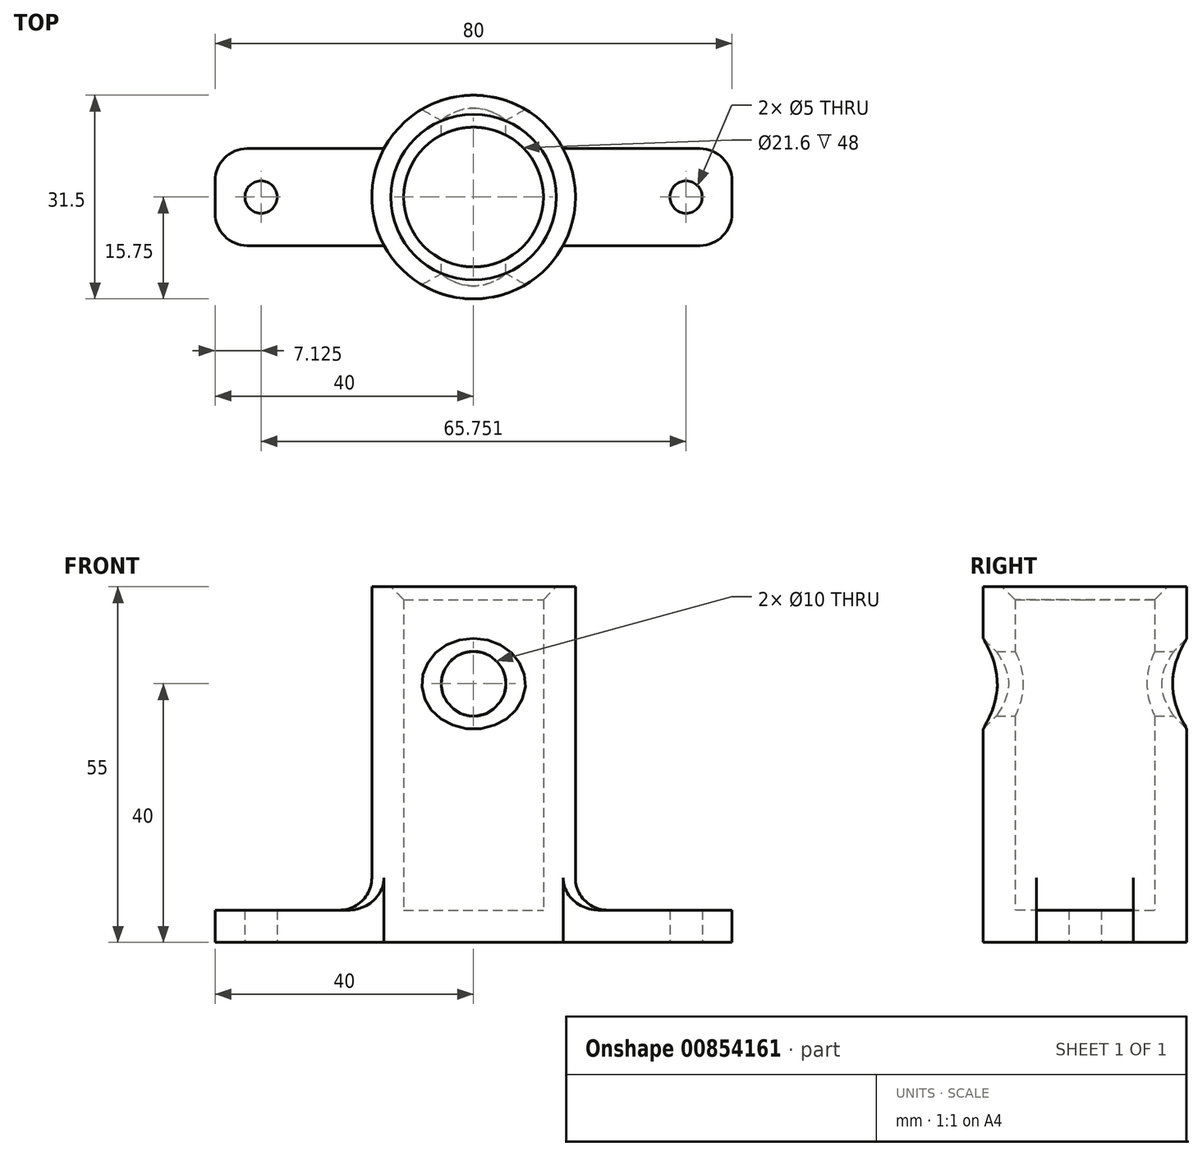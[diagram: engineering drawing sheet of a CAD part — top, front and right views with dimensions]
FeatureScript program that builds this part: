
annotation { "Feature Type Name" : "Feature", "Feature Type Description" : "" }
export const myFeature = defineFeature(function(context is Context, id is Id, definition is map)
    precondition{}
    {
        {
            var Q0;
            Q0=qCreatedBy(makeId("Top.planeOp"),FACE);
            var sketch = newSketch(context, id + "F0", { "sketchPlane" : qUnion([Q0])});
            skCircle(sketch, "E0", {"center": v(0, 0) * mm, "radius": 10.75 * mm});
            skCircle(sketch, "E1.0", {"center": v(0, 0) * mm, "radius": 15.75 * mm});
            skLineSegment(sketch, "E2.bottom", {"start": v(35, -7.5) * mm, "end": v(-35, -7.5) * mm});
            skLineSegment(sketch, "E2.top", {"start": v(35, 7.5) * mm, "end": v(-35, 7.5) * mm});
            skLineSegment(sketch, "E2.left", {"start": v(40, -2.5) * mm, "end": v(40, 2.5) * mm});
            skLineSegment(sketch, "E2.right", {"start": v(-40, -2.5) * mm, "end": v(-40, 2.5) * mm});
            skPoint(sketch, "E3.visualSharp", {"position": v(-40, 7.5) * mm});
            skArc(sketch, "E3.filletArc", {"start": v(-35, 7.5) * mm, "mid": v(-38.54, 6.04) * mm, "end": v(-40, 2.5) * mm});
            skPoint(sketch, "E4.visualSharp", {"position": v(-40, -7.5) * mm});
            skArc(sketch, "E4.filletArc", {"start": v(-40, -2.5) * mm, "mid": v(-38.54, -6.04) * mm, "end": v(-35, -7.5) * mm});
            skPoint(sketch, "E5.visualSharp", {"position": v(40, 7.5) * mm});
            skArc(sketch, "E5.filletArc", {"start": v(40, 2.5) * mm, "mid": v(38.54, 6.04) * mm, "end": v(35, 7.5) * mm});
            skPoint(sketch, "E6.visualSharp", {"position": v(40, -7.5) * mm});
            skArc(sketch, "E6.filletArc", {"start": v(35, -7.5) * mm, "mid": v(38.54, -6.04) * mm, "end": v(40, -2.5) * mm});
            skCircle(sketch, "E7", {"center": v(-32.88, 0) * mm, "radius": 2.5 * mm});
            skCircle(sketch, "E8.MirrorC", {"center": v(32.88, 0) * mm, "radius": 2.5 * mm});
            skSolve(sketch);
        }
        {
            var Q0;
            Q0 = qSketchRegion(id + "F0", true);
            var Q1;
            {var subQ0=sQuery(id+"F0.wireOp",EDGE,"E2.top");var subQ1=sQuery(id+"F0.wireOp",EDGE,"E0");var subQ2=makeQuery(id+"F0.imprint","INTERSECT",VERTEX,{"disambiguationData":[OD(0.0)],"derivedFrom":[subQ1,subQ0]});Q1=makeQuery(id+"F0.imprint","IMPRINT",FACE,{"disambiguationData":[TD([[makeQuery(id+"F0.imprint","IMPRINT",EDGE,{"disambiguationData":[TD([[subQ2,-1.0]])],"derivedFrom":subQ1}),1.0]])]});}
            var Q2;
            {var subQ0=sQuery(id+"F0.wireOp",EDGE,"E2.top");var subQ1=sQuery(id+"F0.wireOp",EDGE,"E0");var subQ2=makeQuery(id+"F0.imprint","INTERSECT",VERTEX,{"disambiguationData":[OD(0.0)],"derivedFrom":[subQ1,subQ0]});Q2=makeQuery(id+"F0.imprint","IMPRINT",FACE,{"disambiguationData":[TD([[makeQuery(id+"F0.imprint","IMPRINT",EDGE,{"disambiguationData":[TD([[subQ2,1.0]])],"derivedFrom":subQ1}),1.0]])]});}
            var Q3;
            {var subQ0=sQuery(id+"F0.wireOp",EDGE,"E2.bottom");var subQ1=sQuery(id+"F0.wireOp",EDGE,"E0");var subQ2=makeQuery(id+"F0.imprint","INTERSECT",VERTEX,{"disambiguationData":[OD(0.0)],"derivedFrom":[subQ1,subQ0]});Q3=makeQuery(id+"F0.imprint","IMPRINT",FACE,{"disambiguationData":[TD([[makeQuery(id+"F0.imprint","IMPRINT",EDGE,{"disambiguationData":[TD([[subQ2,-1.0]])],"derivedFrom":subQ1}),1.0]])]});}
            extrude(context, id + "F1", {"entities" : qUnion([Q0, Q1, Q2, Q3]), "depth" : 5 * mm, "offsetDistance" : 25 * mm});
        }
        {
            var Q0;
            Q0=makeQuery(id+"F1.opExtrude","CAP_FACE",FACE,{"disambiguationData":[OSD([sQuery(id+"F0.wireOp",EDGE,"E1.0"),sQuery(id+"F0.wireOp",EDGE,"E2.bottom"),sQuery(id+"F0.wireOp",EDGE,"E2.top"),sQuery(id+"F0.wireOp",EDGE,"E2.left"),sQuery(id+"F0.wireOp",EDGE,"E2.right"),sQuery(id+"F0.wireOp",EDGE,"E3.filletArc"),sQuery(id+"F0.wireOp",EDGE,"E4.filletArc"),sQuery(id+"F0.wireOp",EDGE,"E5.filletArc"),sQuery(id+"F0.wireOp",EDGE,"E6.filletArc"),sQuery(id+"F0.wireOp",EDGE,"E7"),sQuery(id+"F0.wireOp",EDGE,"E8.MirrorC")])],"isStart":true});
            var sketch = newSketch(context, id + "F2", { "sketchPlane" : qUnion([Q0])});
            skCircle(sketch, "E9", {"center": v(0, 0) * mm, "radius": 15.75 * mm});
            skCircle(sketch, "E10", {"center": v(0, 0) * mm, "radius": 10.8 * mm});
            skSolve(sketch);
        }
        {
            var Q0;
            Q0 = qSketchRegion(id + "F2", true);
            extrude(context, id + "F3", {"entities" : qUnion([Q0]), "operationType" : NewBodyOperationType.ADD, "oppositeDirection" : true, "depth" : 55 * mm, "offsetDistance" : 25 * mm});
        }
        {
            var Q0;
            Q0=makeQuery(id+"F3.boolean.opBoolean","INTERSECT",EDGE,{"disambiguationData":[OD(0.0)],"derivedFrom":[makeQuery(id+"F1.opExtrude","CAP_FACE",FACE,{"disambiguationData":[OSD([sQuery(id+"F0.wireOp",EDGE,"E1.0"),sQuery(id+"F0.wireOp",EDGE,"E2.bottom"),sQuery(id+"F0.wireOp",EDGE,"E2.top"),sQuery(id+"F0.wireOp",EDGE,"E2.left"),sQuery(id+"F0.wireOp",EDGE,"E2.right"),sQuery(id+"F0.wireOp",EDGE,"E3.filletArc"),sQuery(id+"F0.wireOp",EDGE,"E4.filletArc"),sQuery(id+"F0.wireOp",EDGE,"E5.filletArc"),sQuery(id+"F0.wireOp",EDGE,"E6.filletArc"),sQuery(id+"F0.wireOp",EDGE,"E7"),sQuery(id+"F0.wireOp",EDGE,"E8.MirrorC")])],"isStart":false}),makeQuery(id+"F3.opExtrude","SWEPT_FACE",FACE,{"disambiguationData":[OSD([sQuery(id+"F2.wireOp",EDGE,"E9")])]})]});
            var Q1;
            Q1=makeQuery(id+"F3.boolean.opBoolean","INTERSECT",EDGE,{"disambiguationData":[OD(1.0)],"derivedFrom":[makeQuery(id+"F1.opExtrude","CAP_FACE",FACE,{"disambiguationData":[OSD([sQuery(id+"F0.wireOp",EDGE,"E1.0"),sQuery(id+"F0.wireOp",EDGE,"E2.bottom"),sQuery(id+"F0.wireOp",EDGE,"E2.top"),sQuery(id+"F0.wireOp",EDGE,"E2.left"),sQuery(id+"F0.wireOp",EDGE,"E2.right"),sQuery(id+"F0.wireOp",EDGE,"E3.filletArc"),sQuery(id+"F0.wireOp",EDGE,"E4.filletArc"),sQuery(id+"F0.wireOp",EDGE,"E5.filletArc"),sQuery(id+"F0.wireOp",EDGE,"E6.filletArc"),sQuery(id+"F0.wireOp",EDGE,"E7"),sQuery(id+"F0.wireOp",EDGE,"E8.MirrorC")])],"isStart":false}),makeQuery(id+"F3.opExtrude","SWEPT_FACE",FACE,{"disambiguationData":[OSD([sQuery(id+"F2.wireOp",EDGE,"E9")])]})]});
            fillet(context, id + "F4", {"entities" : qUnion([Q0, Q1]), "radius" : 5 * mm, "tangentPropagation" : true, "allowEdgeOverflow" : false});
        }
        {
            var Q0;
            Q0=qCreatedBy(makeId("Front.planeOp"),FACE);
            var sketch = newSketch(context, id + "F5", { "sketchPlane" : qUnion([Q0])});
            skLineSegment(sketch, "E11", {"start": v(0, 0) * mm, "end": v(0, 40) * mm});
            skCircle(sketch, "E12", {"center": v(0, 40) * mm, "radius": 5 * mm});
            skSolve(sketch);
        }
        {
            var Q0;
            Q0=makeQuery(id+"F5.imprint","IMPRINT",FACE,{"disambiguationData":[TD([[makeQuery(id+"F5.imprint","IMPRINT",EDGE,{"derivedFrom":sQuery(id+"F5.wireOp",EDGE,"E12")}),1.0]])]});
            extrude(context, id + "F6", {"entities" : qUnion([Q0]), "operationType" : NewBodyOperationType.REMOVE, "endBound" : BoundingType.SYMMETRIC, "depth" : 60 * mm, "offsetDistance" : 25 * mm});
        }
        {
            var Q0;
            Q0=makeQuery(id+"F3.opExtrude","CAP_EDGE",EDGE,{"disambiguationData":[OSD([sQuery(id+"F2.wireOp",EDGE,"E10")])],"isStart":false});
            var Q1;
            {var subQ0=sQuery(id+"F0.wireOp",EDGE,"E2.bottom");var subQ1=sQuery(id+"F0.wireOp",EDGE,"E1.0");var subQ2=sQuery(id+"F0.wireOp",EDGE,"E2.top");Q1=makeQuery(id+"F6.boolean.opBoolean","INTERSECT",EDGE,{"disambiguationData":[OD(0.0)],"derivedFrom":[makeQuery(id+"F3.boolean.opBoolean","MERGE",FACE,{"derivedFrom":[makeQuery(id+"F1.opExtrude","SWEPT_FACE",FACE,{"disambiguationData":[OSD([subQ1]),TDD([makeQuery(id+"F0.imprint","IMPRINT",EDGE,{"disambiguationData":[TD([[makeQuery(id+"F0.imprint","INTERSECT",VERTEX,{"disambiguationData":[OD(0.0)],"derivedFrom":[subQ1,subQ2]}),1.0]])],"derivedFrom":subQ1})])]}),makeQuery(id+"F1.opExtrude","SWEPT_FACE",FACE,{"disambiguationData":[OSD([subQ1]),TDD([makeQuery(id+"F0.imprint","IMPRINT",EDGE,{"disambiguationData":[TD([[makeQuery(id+"F0.imprint","INTERSECT",VERTEX,{"disambiguationData":[OD(0.0)],"derivedFrom":[subQ1,subQ0]}),-1.0]])],"derivedFrom":subQ1})])]}),makeQuery(id+"F3.opExtrude","SWEPT_FACE",FACE,{"disambiguationData":[OSD([sQuery(id+"F2.wireOp",EDGE,"E9")])]})]}),makeQuery(id+"F6.opExtrude","SWEPT_FACE",FACE,{"disambiguationData":[OSD([sQuery(id+"F5.wireOp",EDGE,"E12")])]})]});}
            var Q2;
            {var subQ0=sQuery(id+"F0.wireOp",EDGE,"E2.bottom");var subQ1=sQuery(id+"F0.wireOp",EDGE,"E1.0");var subQ2=sQuery(id+"F0.wireOp",EDGE,"E2.top");Q2=makeQuery(id+"F6.boolean.opBoolean","INTERSECT",EDGE,{"disambiguationData":[OD(1.0)],"derivedFrom":[makeQuery(id+"F3.boolean.opBoolean","MERGE",FACE,{"derivedFrom":[makeQuery(id+"F1.opExtrude","SWEPT_FACE",FACE,{"disambiguationData":[OSD([subQ1]),TDD([makeQuery(id+"F0.imprint","IMPRINT",EDGE,{"disambiguationData":[TD([[makeQuery(id+"F0.imprint","INTERSECT",VERTEX,{"disambiguationData":[OD(0.0)],"derivedFrom":[subQ1,subQ2]}),1.0]])],"derivedFrom":subQ1})])]}),makeQuery(id+"F1.opExtrude","SWEPT_FACE",FACE,{"disambiguationData":[OSD([subQ1]),TDD([makeQuery(id+"F0.imprint","IMPRINT",EDGE,{"disambiguationData":[TD([[makeQuery(id+"F0.imprint","INTERSECT",VERTEX,{"disambiguationData":[OD(0.0)],"derivedFrom":[subQ1,subQ0]}),-1.0]])],"derivedFrom":subQ1})])]}),makeQuery(id+"F3.opExtrude","SWEPT_FACE",FACE,{"disambiguationData":[OSD([sQuery(id+"F2.wireOp",EDGE,"E9")])]})]}),makeQuery(id+"F6.opExtrude","SWEPT_FACE",FACE,{"disambiguationData":[OSD([sQuery(id+"F5.wireOp",EDGE,"E12")])]})]});}
            chamfer(context, id + "F7", {"entities" : qUnion([Q0, Q1, Q2]), "width" : 2 * mm, "tangentPropagation" : true});
        }
    });
